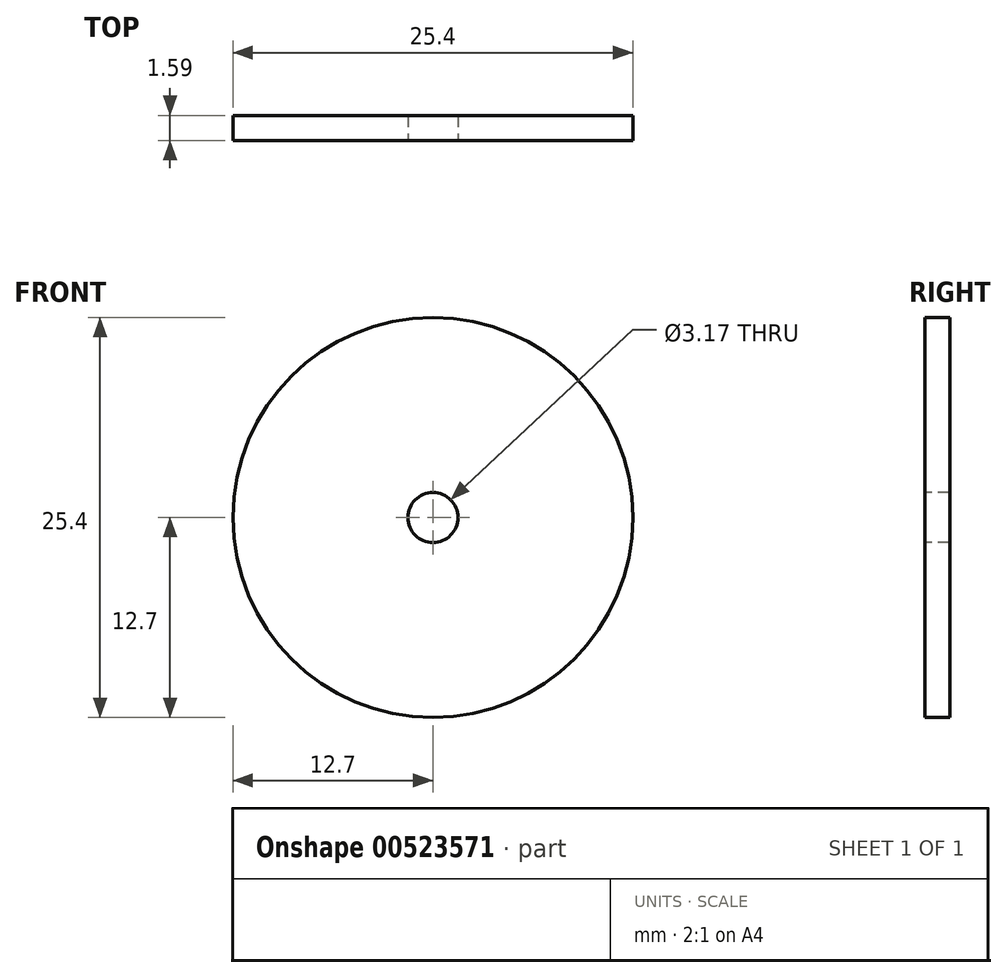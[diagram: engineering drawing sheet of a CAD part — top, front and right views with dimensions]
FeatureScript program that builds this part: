
annotation { "Feature Type Name" : "Feature", "Feature Type Description" : "" }
export const myFeature = defineFeature(function(context is Context, id is Id, definition is map)
    precondition{}
    {
        {
            var Q0;
            Q0=qCreatedBy(makeId("Front.planeOp"),FACE);
            var sketch = newSketch(context, id + "F0", { "sketchPlane" : qUnion([Q0])});
            skCircle(sketch, "E0", {"center": v(0, 0) * mm, "radius": 12.7 * mm});
            skSolve(sketch);
        }
        {
            var Q0;
            Q0=makeQuery(id+"F0.imprint","IMPRINT",FACE,{"disambiguationData":[TD([[makeQuery(id+"F0.imprint","IMPRINT",EDGE,{"derivedFrom":sQuery(id+"F0.wireOp",EDGE,"E0")}),1.0]])]});
            extrude(context, id + "F1", {"entities" : qUnion([Q0]), "depth" : 1.59 * mm, "offsetDistance" : 25.4 * mm});
        }
        {
            var Q0;
            Q0=makeQuery(id+"F1.opExtrude","CAP_FACE",FACE,{"disambiguationData":[OSD([sQuery(id+"F0.wireOp",EDGE,"E0")])],"isStart":false});
            var sketch = newSketch(context, id + "F2", { "sketchPlane" : qUnion([Q0])});
            skPoint(sketch, "E1", {"position": v(0, 0) * mm});
            skSolve(sketch);
        }
        {
            var Q0;
            Q0=sQuery(id+"F2.wireOp",VERTEX,"E1");
            var Q1;
            Q1=makeQuery(id+"F1.opExtrude","SWEPT_BODY",BODY,{"disambiguationData":[OSD([sQuery(id+"F0.wireOp",EDGE,"E0")])]});
            hole(context, id + "F3", {"style" : HoleStyle.SIMPLE, "endStyle" : HoleEndStyle.BLIND, "holeDiameter" : 3.17 * mm, "majorDiameter" : 6.35 * mm, "holeDepth" : 6.35 * mm, "isTappedThrough" : true, "tappedDepth" : 12.7 * mm, "tapClearance" : 3, "locations" : qUnion([Q0]), "scope" : qUnion([Q1])});
        }
    });
